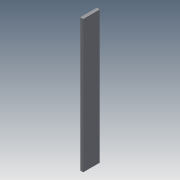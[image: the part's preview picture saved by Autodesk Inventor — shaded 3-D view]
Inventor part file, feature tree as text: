
AUTODESK INVENTOR PART (.ipt)
format: ipt  version: 2015 (Build 190159000, 159)  size: 67,584 bytes
history: native  units: mm
features: extrude x1, sketch x1
ambient origin geometry x8: Origin, YZ Plane, XZ Plane, XY Plane, X Axis, Y Axis, Z Axis, Center Point
bodies: Solid1 (feature_tree)
feature tree (2):
  extrude  "Extrusion1"  Depth=400.0mm
  sketch  "Sketch1"  dims[d0=50.0mm d1=400.0mm d2=9.0mm d3=0.0mm]
